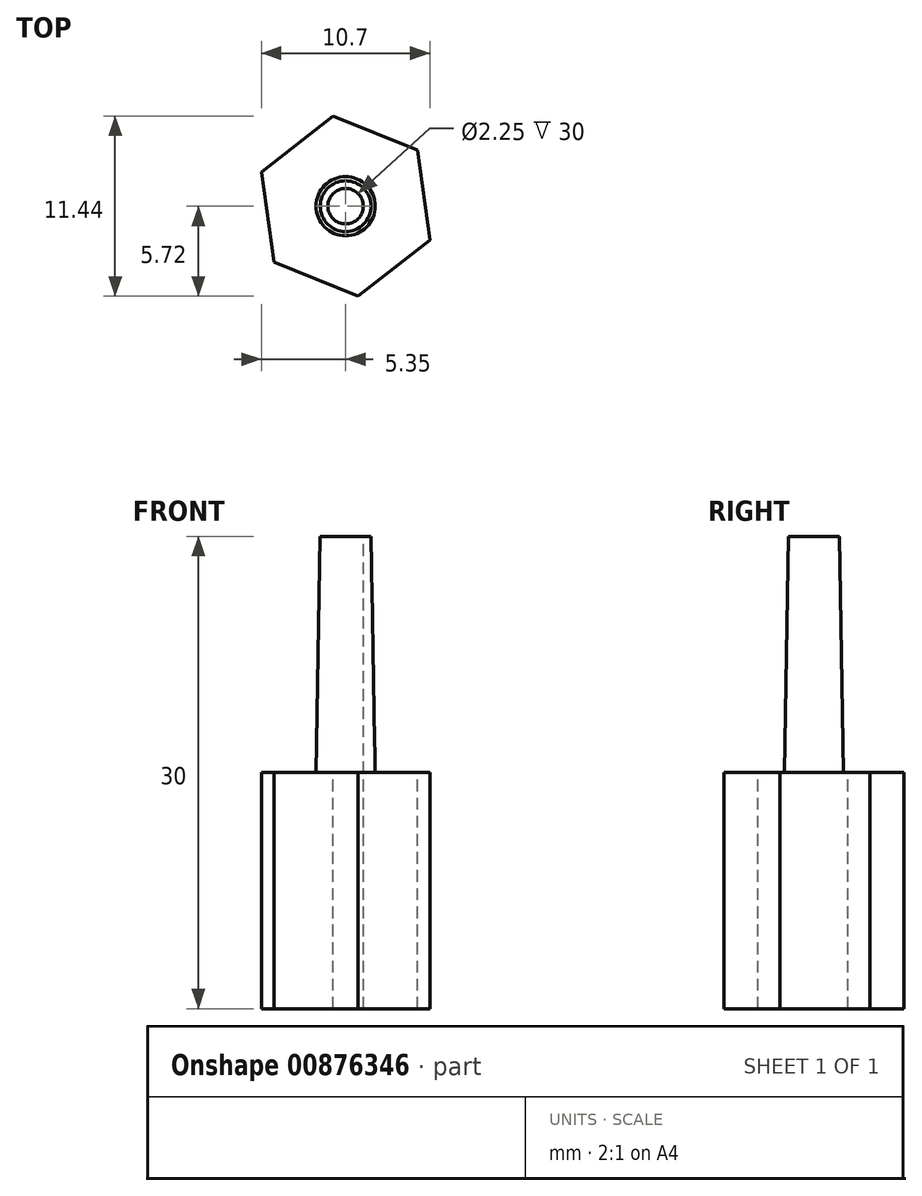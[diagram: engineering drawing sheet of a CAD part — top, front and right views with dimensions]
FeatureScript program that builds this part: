
annotation { "Feature Type Name" : "Feature", "Feature Type Description" : "" }
export const myFeature = defineFeature(function(context is Context, id is Id, definition is map)
    precondition{}
    {
        {
            var Q0;
            Q0=qCreatedBy(makeId("Top.planeOp"),FACE);
            var sketch = newSketch(context, id + "F0", { "sketchPlane" : qUnion([Q0])});
            skCircle(sketch, "E0", {"center": v(0, 0) * mm, "radius": 1.88 * mm});
            skSolve(sketch);
        }
        {
            var Q0;
            Q0 = qSketchRegion(id + "F0", true);
            extrude(context, id + "F1", {"entities" : qUnion([Q0]), "depth" : 15 * mm, "offsetDistance" : 25 * mm, "hasDraft" : true, "draftAngle" : 1 * degree, "draftPullDirection" : true});
        }
        {
            var Q0;
            Q0=qCreatedBy(makeId("Top.planeOp"),FACE);
            var sketch = newSketch(context, id + "F2", { "sketchPlane" : qUnion([Q0])});
            skCircle(sketch, "E1.cCircle", {"center": v(0, 0) * mm, "radius": 5 * mm, "construction": true});
            skLineSegment(sketch, "E1.0", {"start": v(-0.8, 5.72) * mm, "end": v(4.55, 3.55) * mm});
            skLineSegment(sketch, "E1.1", {"start": v(4.55, 3.55) * mm, "end": v(5.35, -2.16) * mm});
            skLineSegment(sketch, "E1.2", {"start": v(5.35, -2.16) * mm, "end": v(0.8, -5.72) * mm});
            skLineSegment(sketch, "E1.3", {"start": v(0.8, -5.72) * mm, "end": v(-4.55, -3.55) * mm});
            skLineSegment(sketch, "E1.4", {"start": v(-4.55, -3.55) * mm, "end": v(-5.35, 2.16) * mm});
            skLineSegment(sketch, "E1.5", {"start": v(-5.35, 2.16) * mm, "end": v(-0.8, 5.72) * mm});
            skPoint(sketch, "E1.0.midPoint", {"position": v(1.87, 4.64) * mm});
            skSolve(sketch);
        }
        {
            var Q0;
            Q0 = qSketchRegion(id + "F2", true);
            extrude(context, id + "F3", {"entities" : qUnion([Q0]), "operationType" : NewBodyOperationType.ADD, "oppositeDirection" : true, "depth" : 15 * mm, "offsetDistance" : 25 * mm});
        }
        {
            var Q0;
            Q0=qCreatedBy(makeId("Top.planeOp"),FACE);
            var sketch = newSketch(context, id + "F4", { "sketchPlane" : qUnion([Q0])});
            skCircle(sketch, "E2", {"center": v(0, 0) * mm, "radius": 1.13 * mm});
            skSolve(sketch);
        }
        {
            var Q0;
            Q0 = qSketchRegion(id + "F4", true);
            extrude(context, id + "F5", {"entities" : qUnion([Q0]), "operationType" : NewBodyOperationType.REMOVE, "oppositeDirection" : true, "depth" : 50 * mm, "offsetDistance" : 25 * mm, "symmetric" : true});
        }
    });
